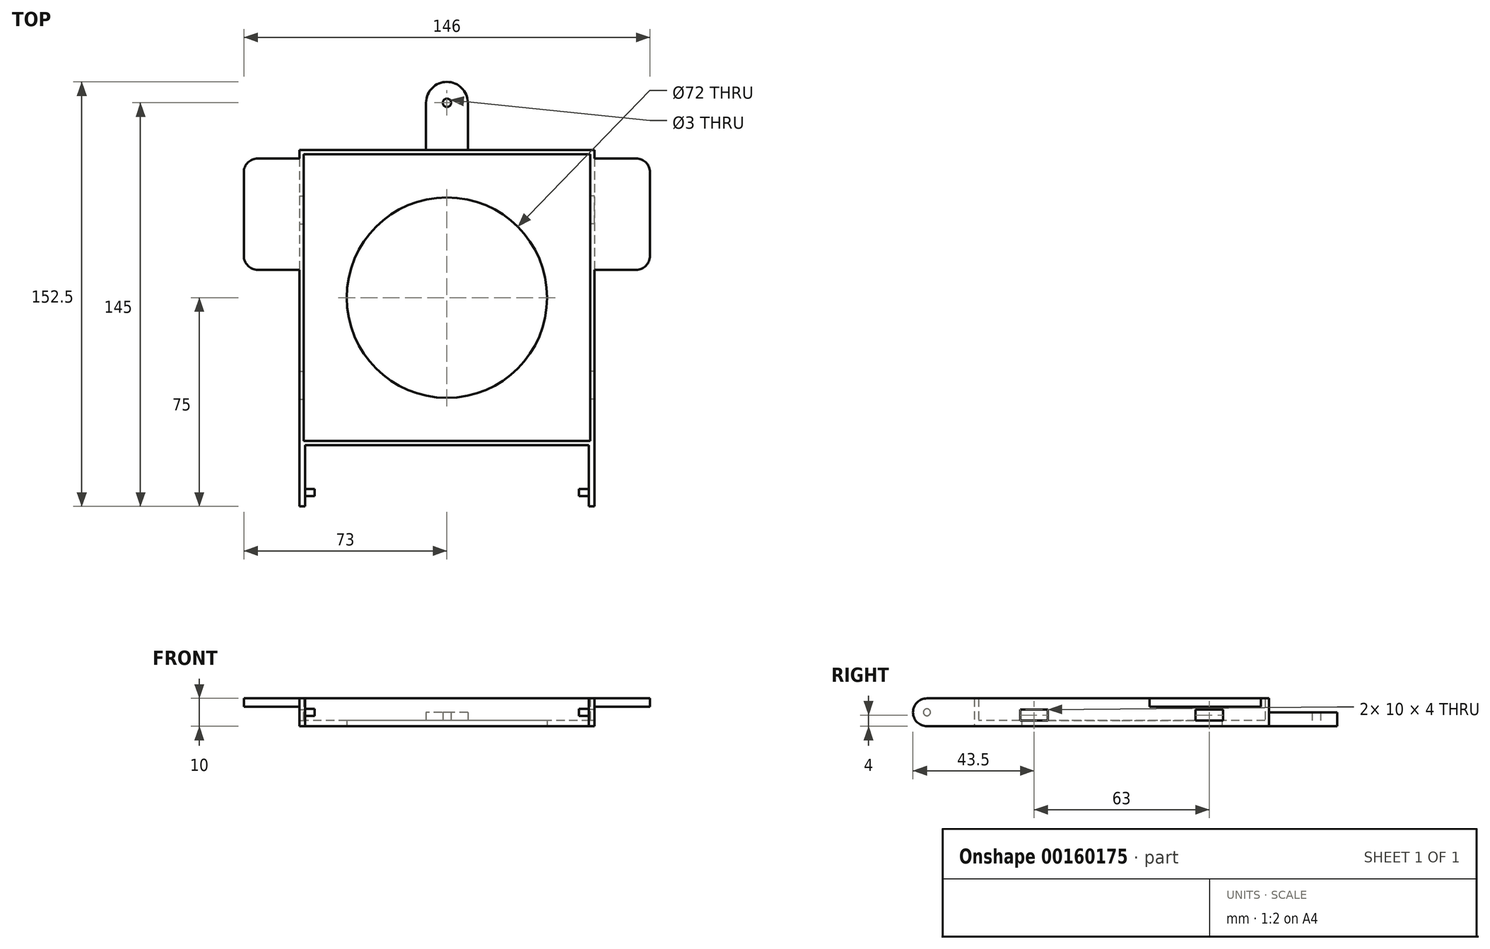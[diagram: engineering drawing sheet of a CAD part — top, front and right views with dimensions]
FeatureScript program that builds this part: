
annotation { "Feature Type Name" : "Feature", "Feature Type Description" : "" }
export const myFeature = defineFeature(function(context is Context, id is Id, definition is map)
    precondition{}
    {
        {
            var Q0;
            Q0=qCreatedBy(makeId("Top.planeOp"),FACE);
            var sketch = newSketch(context, id + "F0", { "sketchPlane" : qUnion([Q0])});
            skLineSegment(sketch, "E0.bottom", {"start": v(51.5, 51.5) * mm, "end": v(-51.5, 51.5) * mm});
            skLineSegment(sketch, "E0.top", {"start": v(51.5, -51.5) * mm, "end": v(-51.5, -51.5) * mm});
            skLineSegment(sketch, "E0.left", {"start": v(51.5, 51.5) * mm, "end": v(51.5, -51.5) * mm});
            skLineSegment(sketch, "E0.right", {"start": v(-51.5, 51.5) * mm, "end": v(-51.5, -51.5) * mm});
            skPoint(sketch, "E0.middle", {"position": v(0, 0) * mm});
            skLineSegment(sketch, "E1.bottom", {"start": v(53, 53) * mm, "end": v(7.5, 53) * mm});
            skLineSegment(sketch, "E1.top", {"start": v(53, -53) * mm, "end": v(-53, -53) * mm});
            skLineSegment(sketch, "E1.left", {"start": v(53, 53) * mm, "end": v(53, -53) * mm});
            skLineSegment(sketch, "E1.right", {"start": v(-53, 53) * mm, "end": v(-53, -53) * mm});
            skCircle(sketch, "E2", {"center": v(0, 0) * mm, "radius": 36 * mm});
            skLineSegment(sketch, "E3.left", {"start": v(7.5, 53) * mm, "end": v(7.5, 70) * mm});
            skLineSegment(sketch, "E3.right", {"start": v(-7.5, 53) * mm, "end": v(-7.5, 70) * mm});
            skLineSegment(sketch, "E4.trimOffspring", {"start": v(-7.5, 53) * mm, "end": v(-53, 53) * mm});
            skArc(sketch, "E5", {"start": v(7.5, 70) * mm, "mid": v(0, 77.5) * mm, "end": v(-7.5, 70) * mm});
            skCircle(sketch, "E6", {"center": v(0, 70) * mm, "radius": 1.5 * mm});
            skLineSegment(sketch, "E7", {"start": v(-7.5, 53) * mm, "end": v(7.5, 53) * mm});
            skSolve(sketch);
        }
        {
            var Q0;
            Q0=makeQuery(id+"F0.imprint","IMPRINT",FACE,{"disambiguationData":[TD([[makeQuery(id+"F0.imprint","IMPRINT",EDGE,{"derivedFrom":sQuery(id+"F0.wireOp",EDGE,"E0.bottom")}),-1.0]])]});
            extrude(context, id + "F1", {"entities" : qUnion([Q0]), "depth" : 10 * mm});
        }
        {
            var Q0;
            Q0=makeQuery(id+"F0.imprint","IMPRINT",FACE,{"disambiguationData":[TD([[makeQuery(id+"F0.imprint","IMPRINT",EDGE,{"derivedFrom":sQuery(id+"F0.wireOp",EDGE,"E0.bottom")}),1.0]])]});
            extrude(context, id + "F2", {"entities" : qUnion([Q0]), "operationType" : NewBodyOperationType.ADD, "depth" : 2 * mm});
        }
        {
            var Q0;
            Q0=makeQuery(id+"F1.opExtrude","SWEPT_FACE",FACE,{"disambiguationData":[OSD([sQuery(id+"F0.wireOp",EDGE,"E0.right")])]});
            var sketch = newSketch(context, id + "F3", { "sketchPlane" : qUnion([Q0])});
            skLineSegment(sketch, "E8.bottom", {"start": v(-36.5, 2) * mm, "end": v(-26.5, 2) * mm});
            skLineSegment(sketch, "E8.top", {"start": v(-36.5, 6) * mm, "end": v(-26.5, 6) * mm});
            skLineSegment(sketch, "E8.left", {"start": v(-36.5, 2) * mm, "end": v(-36.5, 6) * mm});
            skLineSegment(sketch, "E8.right", {"start": v(-26.5, 2) * mm, "end": v(-26.5, 6) * mm});
            skLineSegment(sketch, "E9.bottom", {"start": v(26.5, 2) * mm, "end": v(36.5, 2) * mm});
            skLineSegment(sketch, "E9.top", {"start": v(26.5, 6) * mm, "end": v(36.5, 6) * mm});
            skLineSegment(sketch, "E9.left", {"start": v(26.5, 2) * mm, "end": v(26.5, 6) * mm});
            skLineSegment(sketch, "E9.right", {"start": v(36.5, 2) * mm, "end": v(36.5, 6) * mm});
            skPoint(sketch, "E10", {"position": v(31.5, 6) * mm});
            skSolve(sketch);
        }
        {
            var Q0;
            Q0 = qSketchRegion(id + "F0", true);
            extrude(context, id + "F4", {"entities" : qUnion([Q0]), "operationType" : NewBodyOperationType.ADD, "depth" : 5 * mm});
        }
        {
            var Q0;
            Q0=makeQuery(id+"F3.imprint","IMPRINT",FACE,{"disambiguationData":[TD([[makeQuery(id+"F3.imprint","IMPRINT",EDGE,{"derivedFrom":sQuery(id+"F3.wireOp",EDGE,"E9.bottom")}),-1.0]])]});
            var Q1;
            Q1=makeQuery(id+"F3.imprint","IMPRINT",FACE,{"disambiguationData":[TD([[makeQuery(id+"F3.imprint","IMPRINT",EDGE,{"derivedFrom":sQuery(id+"F3.wireOp",EDGE,"E8.bottom")}),-1.0]])]});
            extrude(context, id + "F5", {"entities" : qUnion([Q0, Q1]), "operationType" : NewBodyOperationType.REMOVE, "oppositeDirection" : true, "depth" : 25 * mm});
        }
        {
            var Q0;
            Q0=makeQuery(id+"F1.opExtrude","SWEPT_FACE",FACE,{"disambiguationData":[OSD([sQuery(id+"F0.wireOp",EDGE,"E0.left")])]});
            var sketch = newSketch(context, id + "F6", { "sketchPlane" : qUnion([Q0])});
            skLineSegment(sketch, "E11.bottom", {"start": v(-36.5, 2) * mm, "end": v(-26.5, 2) * mm});
            skLineSegment(sketch, "E11.top", {"start": v(-36.5, 6) * mm, "end": v(-26.5, 6) * mm});
            skLineSegment(sketch, "E11.left", {"start": v(-36.5, 2) * mm, "end": v(-36.5, 6) * mm});
            skLineSegment(sketch, "E11.right", {"start": v(-26.5, 2) * mm, "end": v(-26.5, 6) * mm});
            skLineSegment(sketch, "E12.bottom", {"start": v(26.5, 2) * mm, "end": v(36.5, 2) * mm});
            skLineSegment(sketch, "E12.top", {"start": v(26.5, 6) * mm, "end": v(36.5, 6) * mm});
            skLineSegment(sketch, "E12.left", {"start": v(26.5, 2) * mm, "end": v(26.5, 6) * mm});
            skLineSegment(sketch, "E12.right", {"start": v(36.5, 2) * mm, "end": v(36.5, 6) * mm});
            skSolve(sketch);
        }
        {
            var Q0;
            Q0 = qSketchRegion(id + "F6", true);
            extrude(context, id + "F7", {"entities" : qUnion([Q0]), "operationType" : NewBodyOperationType.REMOVE, "oppositeDirection" : true, "depth" : 25 * mm});
        }
        {
            var Q0;
            Q0=makeQuery(id+"F1.opExtrude","SWEPT_FACE",FACE,{"disambiguationData":[OSD([sQuery(id+"F0.wireOp",EDGE,"E1.top")])]});
            var sketch = newSketch(context, id + "F8", { "sketchPlane" : qUnion([Q0])});
            skLineSegment(sketch, "E13.bottom", {"start": v(-53, 10) * mm, "end": v(-51, 10) * mm});
            skLineSegment(sketch, "E13.top", {"start": v(-53, 0) * mm, "end": v(-51, 0) * mm});
            skLineSegment(sketch, "E13.left", {"start": v(-53, 10) * mm, "end": v(-53, 0) * mm});
            skLineSegment(sketch, "E13.right", {"start": v(-51, 10) * mm, "end": v(-51, 0) * mm});
            skLineSegment(sketch, "E14.bottom", {"start": v(53, 10) * mm, "end": v(51, 10) * mm});
            skLineSegment(sketch, "E14.top", {"start": v(53, 0) * mm, "end": v(51, 0) * mm});
            skLineSegment(sketch, "E14.left", {"start": v(53, 10) * mm, "end": v(53, 0) * mm});
            skLineSegment(sketch, "E14.right", {"start": v(51, 10) * mm, "end": v(51, 0) * mm});
            skSolve(sketch);
        }
        {
            var Q0;
            Q0 = qSketchRegion(id + "F8", true);
            extrude(context, id + "F9", {"entities" : qUnion([Q0]), "operationType" : NewBodyOperationType.ADD, "depth" : 17 * mm});
        }
        {
            var Q0;
            Q0=makeQuery(id+"F9.boolean.opBoolean","MERGE",FACE,{"derivedFrom":[makeQuery(id+"F1.opExtrude","SWEPT_FACE",FACE,{"disambiguationData":[OSD([sQuery(id+"F0.wireOp",EDGE,"E1.right")])]}),makeQuery(id+"F9.opExtrude","SWEPT_FACE",FACE,{"disambiguationData":[OSD([sQuery(id+"F8.wireOp",EDGE,"E13.left")])]})]});
            var sketch = newSketch(context, id + "F10", { "sketchPlane" : qUnion([Q0])});
            skArc(sketch, "E15", {"start": v(70, 0) * mm, "mid": v(75, 5) * mm, "end": v(70, 10) * mm});
            skSolve(sketch);
        }
        {
            var Q0;
            Q0 = qSketchRegion(id + "F10", true);
            var Q1;
            Q1=makeQuery(id+"F10.imprint","IMPRINT",FACE,{"disambiguationData":[TD([[makeQuery(id+"F10.imprint","IMPRINT",EDGE,{"derivedFrom":sQuery(id+"F10.wireOp",EDGE,"E15")}),1.0]])]});
            extrude(context, id + "F11", {"entities" : qUnion([Q0, Q1]), "operationType" : NewBodyOperationType.ADD, "oppositeDirection" : true, "depth" : 2 * mm});
        }
        {
            var Q0;
            Q0=makeQuery(id+"F9.boolean.opBoolean","MERGE",FACE,{"derivedFrom":[makeQuery(id+"F1.opExtrude","SWEPT_FACE",FACE,{"disambiguationData":[OSD([sQuery(id+"F0.wireOp",EDGE,"E1.left")])]}),makeQuery(id+"F9.opExtrude","SWEPT_FACE",FACE,{"disambiguationData":[OSD([sQuery(id+"F8.wireOp",EDGE,"E14.left")])]})]});
            var sketch = newSketch(context, id + "F12", { "sketchPlane" : qUnion([Q0])});
            skArc(sketch, "E16", {"start": v(-70, 10) * mm, "mid": v(-75, 5) * mm, "end": v(-70, 0) * mm});
            skSolve(sketch);
        }
        {
            var Q0;
            Q0 = qSketchRegion(id + "F12", true);
            var Q1;
            Q1=makeQuery(id+"F12.imprint","IMPRINT",FACE,{"disambiguationData":[TD([[makeQuery(id+"F12.imprint","IMPRINT",EDGE,{"derivedFrom":sQuery(id+"F12.wireOp",EDGE,"E16")}),1.0]])]});
            extrude(context, id + "F13", {"entities" : qUnion([Q0, Q1]), "operationType" : NewBodyOperationType.ADD, "oppositeDirection" : true, "depth" : 2 * mm});
        }
        {
            var Q0;
            Q0=makeQuery(id+"F11.boolean.opBoolean","MERGE",FACE,{"derivedFrom":[makeQuery(id+"F9.opExtrude","SWEPT_FACE",FACE,{"disambiguationData":[OSD([sQuery(id+"F8.wireOp",EDGE,"E13.right")])]}),makeQuery(id+"F11.opExtrude","CAP_FACE",FACE,{"disambiguationData":[OSD([sQuery(id+"F8.wireOp",EDGE,"E13.left"),sQuery(id+"F10.wireOp",EDGE,"E15")])],"isStart":false})]});
            var sketch = newSketch(context, id + "F14", { "sketchPlane" : qUnion([Q0])});
            skCircle(sketch, "E17", {"center": v(-70, 5) * mm, "radius": 1.25 * mm});
            skSolve(sketch);
        }
        {
            var Q0;
            Q0 = qSketchRegion(id + "F14", true);
            extrude(context, id + "F15", {"entities" : qUnion([Q0]), "operationType" : NewBodyOperationType.ADD, "depth" : 3.5 * mm});
        }
        {
            var Q0;
            Q0=makeQuery(id+"F13.boolean.opBoolean","MERGE",FACE,{"derivedFrom":[makeQuery(id+"F9.opExtrude","SWEPT_FACE",FACE,{"disambiguationData":[OSD([sQuery(id+"F8.wireOp",EDGE,"E14.right")])]}),makeQuery(id+"F13.opExtrude","CAP_FACE",FACE,{"disambiguationData":[OSD([sQuery(id+"F8.wireOp",EDGE,"E14.left"),sQuery(id+"F12.wireOp",EDGE,"E16")])],"isStart":false})]});
            var sketch = newSketch(context, id + "F16", { "sketchPlane" : qUnion([Q0])});
            skCircle(sketch, "E18", {"center": v(70, 5) * mm, "radius": 1.25 * mm});
            skSolve(sketch);
        }
        {
            var Q0;
            Q0 = qSketchRegion(id + "F16", true);
            extrude(context, id + "F17", {"entities" : qUnion([Q0]), "operationType" : NewBodyOperationType.ADD, "depth" : 3.5 * mm});
        }
        {
            var Q0;
            Q0=makeQuery(id+"F9.boolean.opBoolean","MERGE",FACE,{"derivedFrom":[makeQuery(id+"F1.opExtrude","CAP_FACE",FACE,{"disambiguationData":[OSD([sQuery(id+"F0.wireOp",EDGE,"E0.bottom"),sQuery(id+"F0.wireOp",EDGE,"E0.top"),sQuery(id+"F0.wireOp",EDGE,"E0.left"),sQuery(id+"F0.wireOp",EDGE,"E0.right"),sQuery(id+"F0.wireOp",EDGE,"E1.bottom"),sQuery(id+"F0.wireOp",EDGE,"E1.top"),sQuery(id+"F0.wireOp",EDGE,"E1.left"),sQuery(id+"F0.wireOp",EDGE,"E1.right"),sQuery(id+"F0.wireOp",EDGE,"E4.trimOffspring"),sQuery(id+"F0.wireOp",EDGE,"E7")])],"isStart":false}),makeQuery(id+"F9.opExtrude","SWEPT_FACE",FACE,{"disambiguationData":[OSD([sQuery(id+"F8.wireOp",EDGE,"E13.bottom")])]}),makeQuery(id+"F9.opExtrude","SWEPT_FACE",FACE,{"disambiguationData":[OSD([sQuery(id+"F8.wireOp",EDGE,"E14.bottom")])]})]});
            var sketch = newSketch(context, id + "F18", { "sketchPlane" : qUnion([Q0])});
            skLineSegment(sketch, "E19.bottom", {"start": v(53, 50) * mm, "end": v(68, 50) * mm});
            skLineSegment(sketch, "E19.top", {"start": v(53, 10) * mm, "end": v(68, 10) * mm});
            skLineSegment(sketch, "E19.left", {"start": v(53, 50) * mm, "end": v(53, 10) * mm});
            skLineSegment(sketch, "E19.right", {"start": v(73, 45) * mm, "end": v(73, 15) * mm});
            skPoint(sketch, "E20.visualSharp", {"position": v(73, 50) * mm});
            skArc(sketch, "E20.filletArc", {"start": v(73, 45) * mm, "mid": v(71.54, 48.54) * mm, "end": v(68, 50) * mm});
            skPoint(sketch, "E21.visualSharp", {"position": v(73, 10) * mm});
            skArc(sketch, "E21.filletArc", {"start": v(68, 10) * mm, "mid": v(71.54, 11.46) * mm, "end": v(73, 15) * mm});
            skSolve(sketch);
        }
        {
            var Q0;
            Q0 = qSketchRegion(id + "F18", true);
            extrude(context, id + "F19", {"entities" : qUnion([Q0]), "oppositeDirection" : true, "depth" : 3 * mm});
        }
        {
            var Q0;
            Q0=makeQuery(id+"F19.opExtrude","SWEPT_BODY",BODY,{"disambiguationData":[OSD([sQuery(id+"F18.wireOp",EDGE,"E19.bottom"),sQuery(id+"F18.wireOp",EDGE,"E19.top"),sQuery(id+"F18.wireOp",EDGE,"E19.left"),sQuery(id+"F18.wireOp",EDGE,"E19.right"),sQuery(id+"F18.wireOp",EDGE,"E20.filletArc"),sQuery(id+"F18.wireOp",EDGE,"E21.filletArc")])]});
            var Q1;
            Q1=qCreatedBy(makeId("Right.planeOp"),FACE);
            mirror(context, id + "F20", {"operationType" : NewBodyOperationType.ADD, "entities" : qUnion([Q0]), "mirrorPlane" : qUnion([Q1])});
        }
    });
